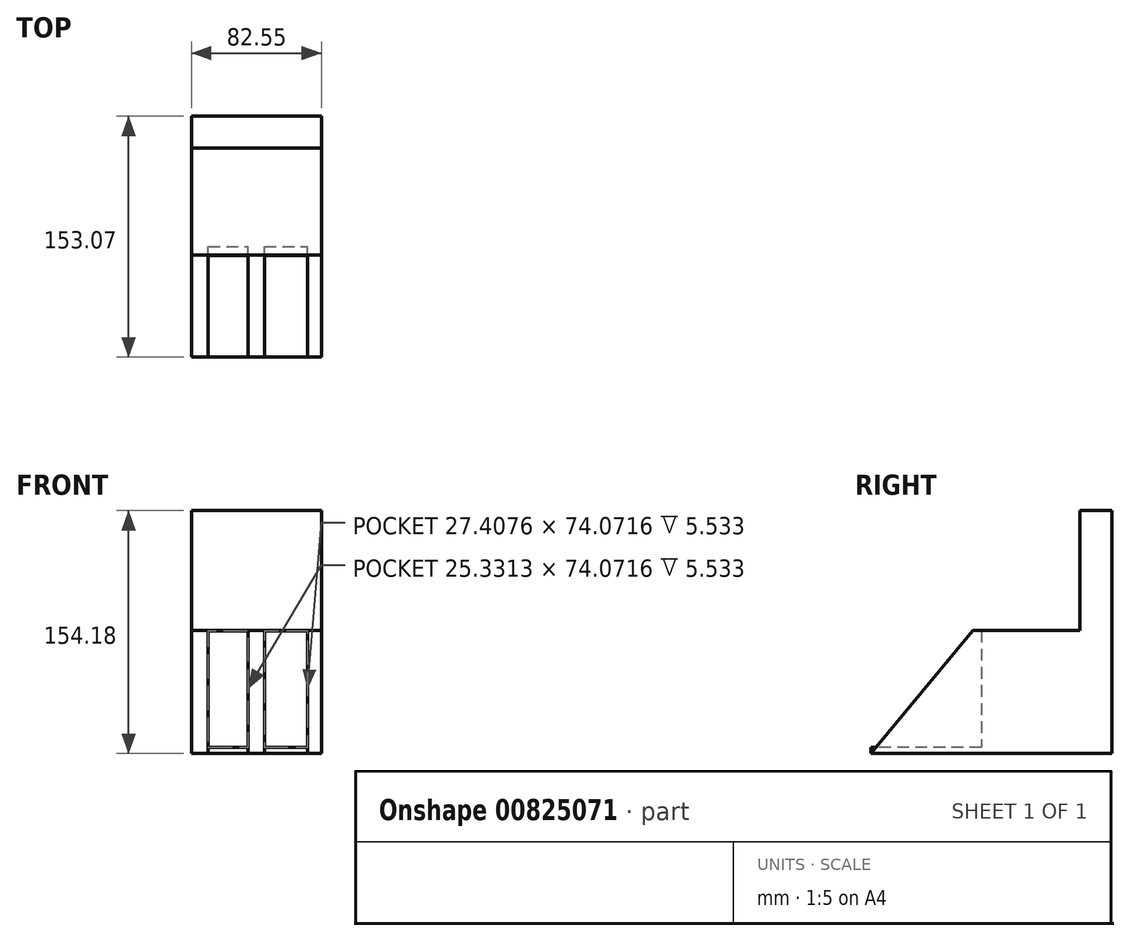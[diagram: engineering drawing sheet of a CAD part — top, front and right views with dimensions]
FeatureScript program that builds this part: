
annotation { "Feature Type Name" : "Feature", "Feature Type Description" : "" }
export const myFeature = defineFeature(function(context is Context, id is Id, definition is map)
    precondition{}
    {
        {
            var Q0;
            Q0=qCreatedBy(makeId("Right.planeOp"),FACE);
            var sketch = newSketch(context, id + "F0", { "sketchPlane" : qUnion([Q0])});
            skLineSegment(sketch, "E0", {"start": v(-70.19, -26.1) * mm, "end": v(62.56, -26.1) * mm});
            skLineSegment(sketch, "E1", {"start": v(62.56, -26.1) * mm, "end": v(62.56, 52.06) * mm});
            skLineSegment(sketch, "E2", {"start": v(62.56, 52.06) * mm, "end": v(-5.3, 52.06) * mm});
            skLineSegment(sketch, "E3", {"start": v(-5.3, 52.06) * mm, "end": v(-70.19, -26.1) * mm});
            skSolve(sketch);
        }
        {
            var Q0;
            Q0 = qSketchRegion(id + "F0", true);
            extrude(context, id + "F1", {"entities" : qUnion([Q0]), "oppositeDirection" : true, "depth" : 82.55 * mm, "offsetDistance" : 25.4 * mm});
        }
        {
            var Q0;
            Q0=makeQuery(id+"F1.opExtrude","SWEPT_FACE",FACE,{"disambiguationData":[OSD([sQuery(id+"F0.wireOp",EDGE,"E1")])]});
            var sketch = newSketch(context, id + "F2", { "sketchPlane" : qUnion([Q0])});
            skLineSegment(sketch, "E4", {"start": v(0, -26.1) * mm, "end": v(0, 128.07) * mm});
            skPoint(sketch, "E4.endSnap0", {"position": v(0, 12.98) * mm});
            skLineSegment(sketch, "E5", {"start": v(0, 128.07) * mm, "end": v(82.55, 128.07) * mm});
            skLineSegment(sketch, "E6", {"start": v(82.55, 128.07) * mm, "end": v(82.55, -26.1) * mm});
            skLineSegment(sketch, "E7", {"start": v(82.55, -26.1) * mm, "end": v(0, -26.1) * mm});
            skSolve(sketch);
        }
        {
            var Q0;
            Q0 = qSketchRegion(id + "F2", true);
            extrude(context, id + "F3", {"entities" : qUnion([Q0]), "operationType" : NewBodyOperationType.ADD, "depth" : 20.32 * mm, "offsetDistance" : 25.4 * mm});
        }
        {
            var Q0;
            Q0=qCreatedBy(makeId("Front.planeOp"),FACE);
            var sketch = newSketch(context, id + "F4", { "sketchPlane" : qUnion([Q0])});
            skLineSegment(sketch, "E8.bottom", {"start": v(-71.88, 51.77) * mm, "end": v(-46.55, 51.77) * mm});
            skLineSegment(sketch, "E8.top", {"start": v(-71.88, -26.3) * mm, "end": v(-46.55, -26.3) * mm});
            skLineSegment(sketch, "E8.left", {"start": v(-71.88, 51.77) * mm, "end": v(-71.88, -26.3) * mm});
            skLineSegment(sketch, "E8.right", {"start": v(-46.55, 51.77) * mm, "end": v(-46.55, -26.3) * mm});
            skLineSegment(sketch, "E9.bottom", {"start": v(-36.16, 51.77) * mm, "end": v(-8.76, 51.77) * mm});
            skLineSegment(sketch, "E9.top", {"start": v(-36.16, -26.3) * mm, "end": v(-8.76, -26.3) * mm});
            skLineSegment(sketch, "E9.left", {"start": v(-36.16, 51.77) * mm, "end": v(-36.16, -26.3) * mm});
            skLineSegment(sketch, "E9.right", {"start": v(-8.76, 51.77) * mm, "end": v(-8.76, -26.3) * mm});
            skSolve(sketch);
        }
        {
            var Q0;
            Q0 = qSketchRegion(id + "F4", true);
            extrude(context, id + "F5", {"entities" : qUnion([Q0]), "operationType" : NewBodyOperationType.REMOVE, "depth" : 76.2 * mm, "offsetDistance" : 25.4 * mm});
        }
        {
            var Q0;
            Q0=makeQuery(id+"F3.boolean.opBoolean","MERGE",FACE,{"derivedFrom":[makeQuery(id+"F1.opExtrude","SWEPT_FACE",FACE,{"disambiguationData":[OSD([sQuery(id+"F0.wireOp",EDGE,"E0")])]}),makeQuery(id+"F3.opExtrude","SWEPT_FACE",FACE,{"disambiguationData":[OSD([sQuery(id+"F2.wireOp",EDGE,"E7")])]})]});
            var sketch = newSketch(context, id + "F6", { "sketchPlane" : qUnion([Q0])});
            skLineSegment(sketch, "E10.bottom", {"start": v(-82.55, 70.19) * mm, "end": v(0, 70.19) * mm});
            skLineSegment(sketch, "E10.top", {"start": v(-82.55, 0) * mm, "end": v(0, 0) * mm});
            skLineSegment(sketch, "E10.left", {"start": v(-82.55, 70.19) * mm, "end": v(-82.55, 0) * mm});
            skLineSegment(sketch, "E10.right", {"start": v(0, 70.19) * mm, "end": v(0, 0) * mm});
            skSolve(sketch);
        }
        {
            var Q0;
            {var subQ1=makeQuery(id+"F3.boolean.opBoolean","MERGE",FACE,{"derivedFrom":[makeQuery(id+"F1.opExtrude","SWEPT_FACE",FACE,{"disambiguationData":[OSD([sQuery(id+"F0.wireOp",EDGE,"E0")])]}),makeQuery(id+"F3.opExtrude","SWEPT_FACE",FACE,{"disambiguationData":[OSD([sQuery(id+"F2.wireOp",EDGE,"E7")])]})]});var subQ2=makeQuery(id+"F5.boolean.opBoolean","INTERSECT",EDGE,{"derivedFrom":[subQ1,makeQuery(id+"F5.opExtrude","SWEPT_FACE",FACE,{"disambiguationData":[OSD([sQuery(id+"F4.wireOp",EDGE,"E8.left")])]})]});Q0=makeQuery(id+"F6.imprint","IMPRINT",FACE,{"disambiguationData":[TD([[makeQuery(id+"F6.imprint","IMPRINT",EDGE,{"derivedFrom":subQ2}),-1.0]])]});}
            var Q1;
            {var subQ1=makeQuery(id+"F3.boolean.opBoolean","MERGE",FACE,{"derivedFrom":[makeQuery(id+"F1.opExtrude","SWEPT_FACE",FACE,{"disambiguationData":[OSD([sQuery(id+"F0.wireOp",EDGE,"E0")])]}),makeQuery(id+"F3.opExtrude","SWEPT_FACE",FACE,{"disambiguationData":[OSD([sQuery(id+"F2.wireOp",EDGE,"E7")])]})]});var subQ2=makeQuery(id+"F5.boolean.opBoolean","INTERSECT",EDGE,{"derivedFrom":[subQ1,makeQuery(id+"F5.opExtrude","SWEPT_FACE",FACE,{"disambiguationData":[OSD([sQuery(id+"F4.wireOp",EDGE,"E9.left")])]})]});Q1=makeQuery(id+"F6.imprint","IMPRINT",FACE,{"disambiguationData":[TD([[makeQuery(id+"F6.imprint","IMPRINT",EDGE,{"derivedFrom":subQ2}),-1.0]])]});}
            extrude(context, id + "F7", {"entities" : qUnion([Q0, Q1]), "operationType" : NewBodyOperationType.ADD, "oppositeDirection" : true, "depth" : 3.8 * mm, "offsetDistance" : 25.4 * mm});
        }
    });
